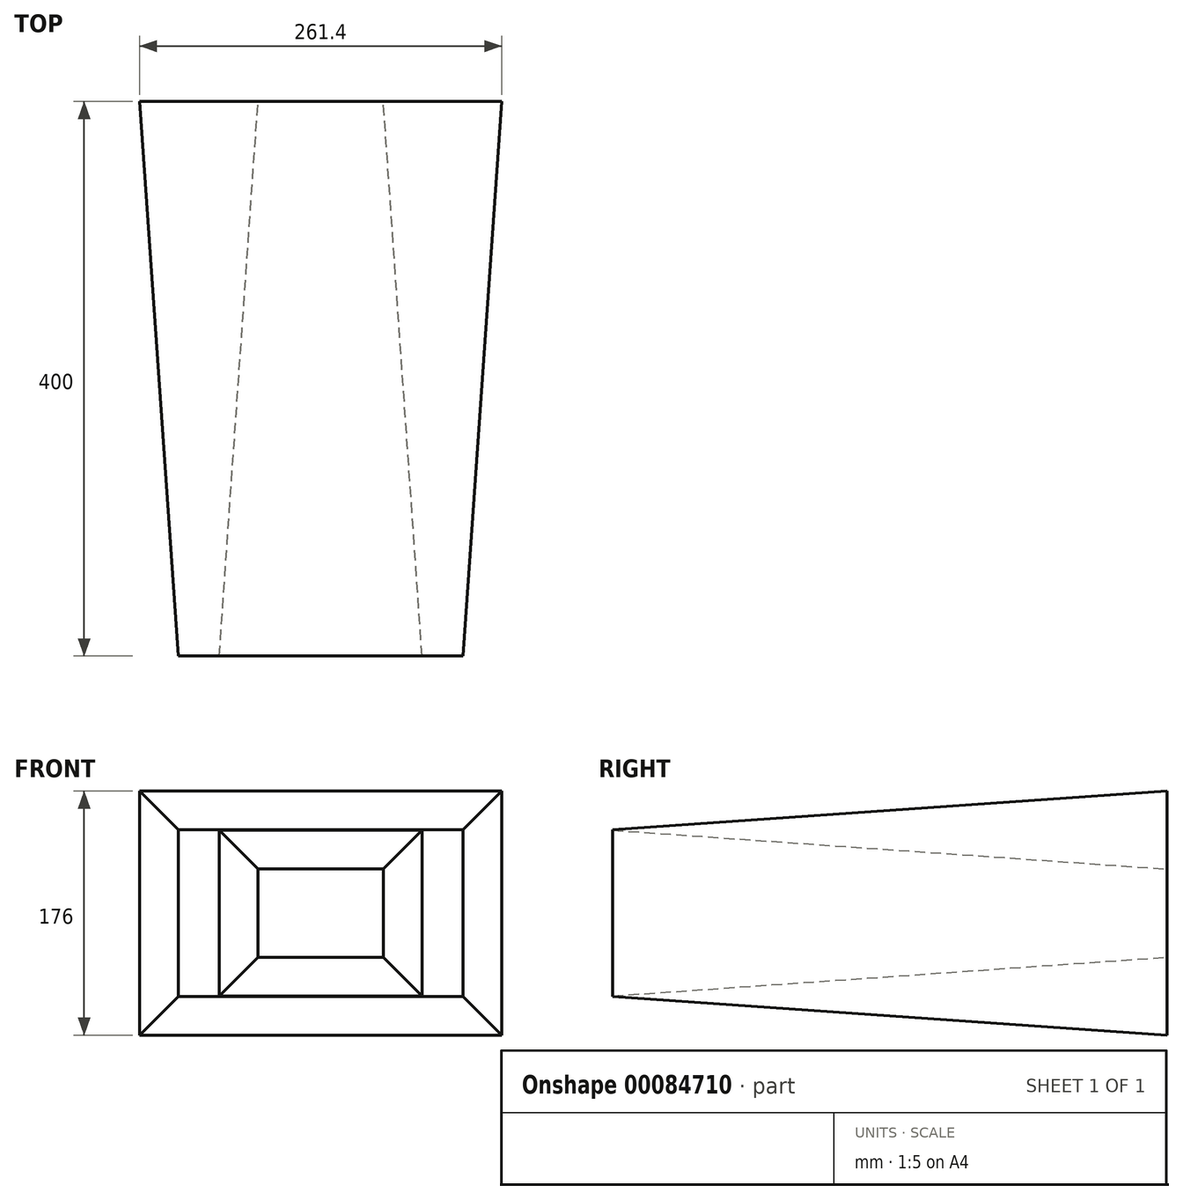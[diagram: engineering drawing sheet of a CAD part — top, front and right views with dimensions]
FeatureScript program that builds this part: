
annotation { "Feature Type Name" : "Feature", "Feature Type Description" : "" }
export const myFeature = defineFeature(function(context is Context, id is Id, definition is map)
    precondition{}
    {
        {
            var Q0;
            Q0=qCreatedBy(makeId("Front.planeOp"),FACE);
            var sketch = newSketch(context, id + "F0", { "sketchPlane" : qUnion([Q0])});
            skLineSegment(sketch, "E0", {"start": v(-45.2, 31.8) * mm, "end": v(45.2, 31.8) * mm});
            skLineSegment(sketch, "E1", {"start": v(45.2, 31.8) * mm, "end": v(45.2, -31.8) * mm});
            skLineSegment(sketch, "E2", {"start": v(45.2, -31.8) * mm, "end": v(-45.2, -31.8) * mm});
            skLineSegment(sketch, "E3", {"start": v(-45.2, -31.8) * mm, "end": v(-45.2, 31.8) * mm});
            skLineSegment(sketch, "E4", {"start": v(-45.2, 0) * mm, "end": v(45.2, 0) * mm, "construction": true});
            skLineSegment(sketch, "E5.bottom", {"start": v(-130.7, 88) * mm, "end": v(130.7, 88) * mm});
            skLineSegment(sketch, "E5.top", {"start": v(-130.7, -88) * mm, "end": v(130.7, -88) * mm});
            skLineSegment(sketch, "E5.left", {"start": v(-130.7, 88) * mm, "end": v(-130.7, -88) * mm});
            skLineSegment(sketch, "E5.right", {"start": v(130.7, 88) * mm, "end": v(130.7, -88) * mm});
            skLineSegment(sketch, "E6", {"start": v(0, -88) * mm, "end": v(0, 88) * mm, "construction": true});
            skLineSegment(sketch, "E7", {"start": v(45.2, 31.8) * mm, "end": v(130.7, 88) * mm});
            skLineSegment(sketch, "E8", {"start": v(-45.2, 31.8) * mm, "end": v(-130.7, 88) * mm});
            skLineSegment(sketch, "E9", {"start": v(-45.2, -31.8) * mm, "end": v(-130.7, -88) * mm});
            skLineSegment(sketch, "E10", {"start": v(45.2, -31.8) * mm, "end": v(130.7, -88) * mm});
            skSolve(sketch);
        }
        {
            var Q0;
            Q0=qCreatedBy(makeId("Front.planeOp"),FACE);
            cPlane(context, id + "F1", {"entities" : qUnion([Q0]), "cplaneType" : CPlaneType.OFFSET, "offset" : 400 * mm, "width" : 150 * mm, "height" : 150 * mm});
        }
        {
            var Q0;
            Q0=makeQuery(id+"F0.imprint","IMPRINT",FACE,{"disambiguationData":[TD([[makeQuery(id+"F0.imprint","IMPRINT",EDGE,{"derivedFrom":sQuery(id+"F0.wireOp",EDGE,"E0")}),1.0]])]});
            var Q1;
            Q1=makeQuery(id+"F0.imprint","IMPRINT",FACE,{"disambiguationData":[TD([[makeQuery(id+"F0.imprint","IMPRINT",EDGE,{"derivedFrom":sQuery(id+"F0.wireOp",EDGE,"E1")}),1.0]])]});
            var Q2;
            Q2=makeQuery(id+"F0.imprint","IMPRINT",FACE,{"disambiguationData":[TD([[makeQuery(id+"F0.imprint","IMPRINT",EDGE,{"derivedFrom":sQuery(id+"F0.wireOp",EDGE,"E2")}),1.0]])]});
            var Q3;
            Q3=makeQuery(id+"F0.imprint","IMPRINT",FACE,{"disambiguationData":[TD([[makeQuery(id+"F0.imprint","IMPRINT",EDGE,{"derivedFrom":sQuery(id+"F0.wireOp",EDGE,"E3")}),1.0]])]});
            extrude(context, id + "F2", {"entities" : qUnion([Q0, Q1, Q2, Q3]), "depth" : 400 * mm, "hasDraft" : true, "draftAngle" : 4 * degree, "draftPullDirection" : true});
        }
    });
